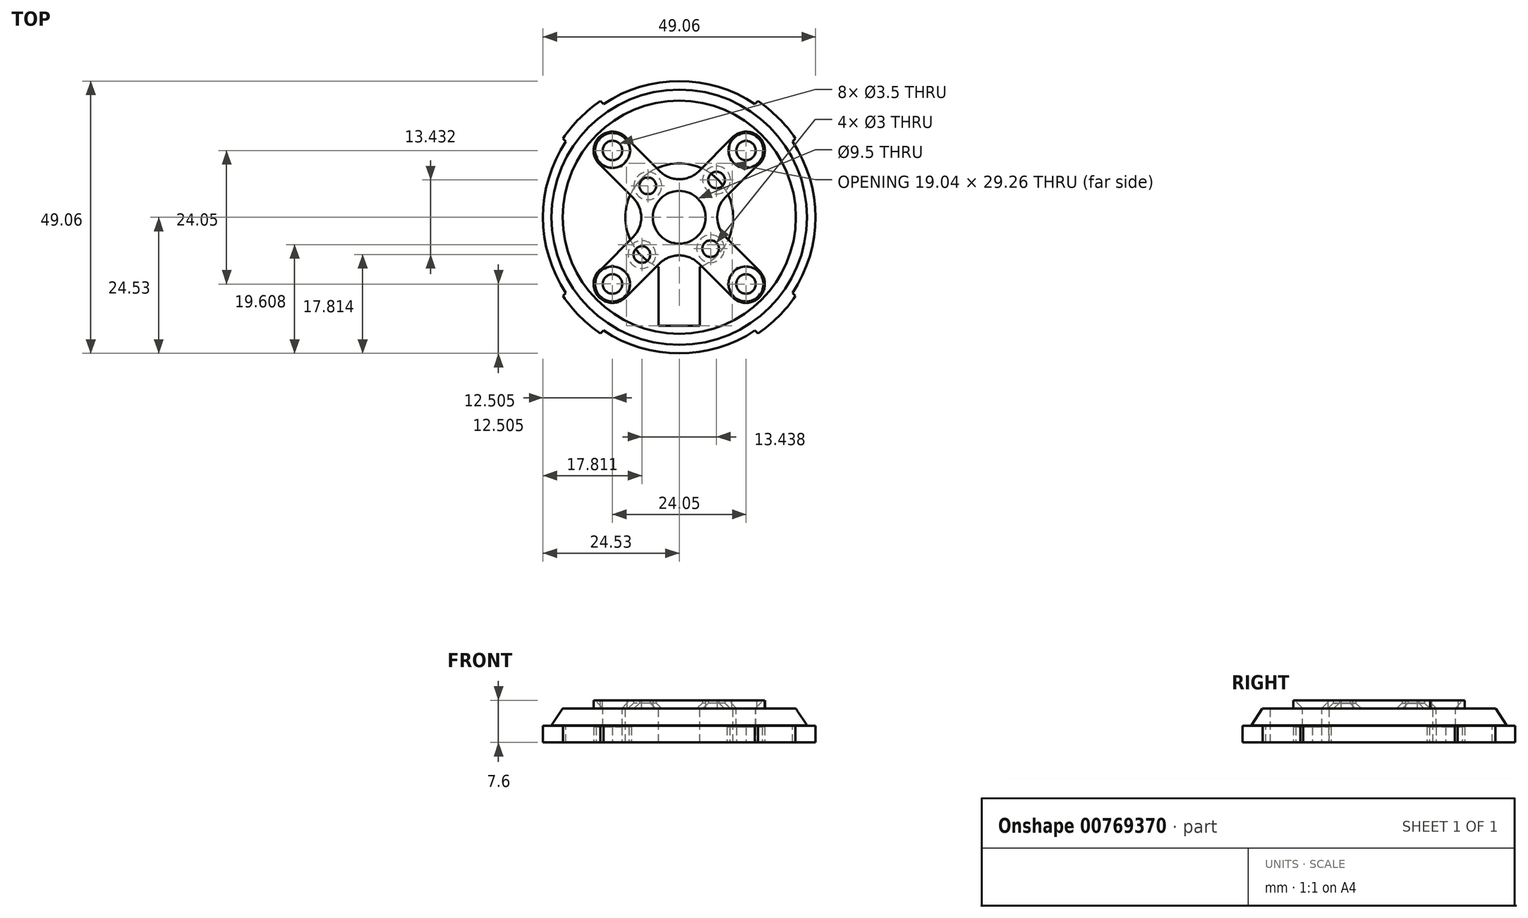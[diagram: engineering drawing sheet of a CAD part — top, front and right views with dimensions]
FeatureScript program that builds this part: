
annotation { "Feature Type Name" : "Feature", "Feature Type Description" : "" }
export const myFeature = defineFeature(function(context is Context, id is Id, definition is map)
    precondition{}
    {
        {
            var Q0;
            Q0=qCreatedBy(makeId("Top.planeOp"),FACE);
            var sketch = newSketch(context, id + "F0", { "sketchPlane" : qUnion([Q0])});
            skCircle(sketch, "E0", {"center": v(0, 0) * mm, "radius": 24.53 * mm});
            skSolve(sketch);
        }
        {
            var Q0;
            Q0=qSketchRegion(id+"F0",true);
            extrude(context, id + "F1", {"entities" : qUnion([Q0]), "oppositeDirection" : true, "depth" : 3 * mm});
        }
        {
            var Q0;
            Q0=makeQuery(id+"F1.opExtrude","CAP_FACE",FACE,{"disambiguationData":[OSD([sQuery(id+"F0.wireOp",EDGE,"E0")])],"isStart":true});
            var sketch = newSketch(context, id + "F2", { "sketchPlane" : qUnion([Q0])});
            skCircle(sketch, "E1", {"center": v(0, 0) * mm, "radius": 23 * mm});
            skSolve(sketch);
        }
        {
            var Q0;
            Q0=qSketchRegion(id+"F2",true);
            extrude(context, id + "F3", {"entities" : qUnion([Q0]), "operationType" : NewBodyOperationType.ADD, "depth" : 3.1 * mm});
        }
        {
            var Q0;
            Q0=makeQuery(id+"F3.opExtrude","CAP_EDGE",EDGE,{"disambiguationData":[OSD([sQuery(id+"F2.wireOp",EDGE,"E1")])],"isStart":false});
            chamfer(context, id + "F4", {"entities" : qUnion([Q0]), "chamferType" : ChamferType.TWO_OFFSETS, "width1" : 2 * mm, "oppositeDirection" : false, "width2" : 3 * mm, "tangentPropagation" : true});
        }
        {
            var Q0;
            Q0=makeQuery(id+"F3.opExtrude","CAP_FACE",FACE,{"disambiguationData":[OSD([sQuery(id+"F2.wireOp",EDGE,"E1")])],"isStart":false});
            var sketch = newSketch(context, id + "F5", { "sketchPlane" : qUnion([Q0])});
            skLineSegment(sketch, "E2.bottom", {"start": v(-12.02, 12.02) * mm, "end": v(12.02, 12.02) * mm, "construction": true});
            skLineSegment(sketch, "E2.top", {"start": v(-12.02, -12.02) * mm, "end": v(12.02, -12.02) * mm, "construction": true});
            skLineSegment(sketch, "E2.left", {"start": v(-12.02, 12.02) * mm, "end": v(-12.02, -12.02) * mm, "construction": true});
            skLineSegment(sketch, "E2.right", {"start": v(12.02, 12.02) * mm, "end": v(12.02, -12.02) * mm, "construction": true});
            skPoint(sketch, "E2.middle", {"position": v(0, 0) * mm});
            skCircle(sketch, "E3", {"center": v(-12.02, 12.02) * mm, "radius": 1.75 * mm});
            skCircle(sketch, "E4.1.0", {"center": v(-12.02, -12.02) * mm, "radius": 1.75 * mm});
            skCircle(sketch, "E4.2.0", {"center": v(12.02, -12.02) * mm, "radius": 1.75 * mm});
            skCircle(sketch, "E4.3.0", {"center": v(12.02, 12.02) * mm, "radius": 1.75 * mm});
            skSolve(sketch);
        }
        {
            var Q0;
            Q0=makeQuery(id+"F5.imprint","IMPRINT",FACE,{"disambiguationData":[TD([[makeQuery(id+"F5.imprint","IMPRINT",EDGE,{"derivedFrom":sQuery(id+"F5.wireOp",EDGE,"E3")}),-1.0]])]});
            var sketch = newSketch(context, id + "F6", { "sketchPlane" : qUnion([Q0])});
            skArc(sketch, "E5", {"start": v(3.71, -8.97) * mm, "mid": v(0, 9.7) * mm, "end": v(-3.71, -8.97) * mm});
            skLineSegment(sketch, "E6.top", {"start": v(-3.71, -19.55) * mm, "end": v(3.71, -19.55) * mm});
            skLineSegment(sketch, "E6.left", {"start": v(-3.71, -8.97) * mm, "end": v(-3.71, -19.55) * mm});
            skLineSegment(sketch, "E6.right", {"start": v(3.71, -8.97) * mm, "end": v(3.71, -19.55) * mm});
            skSolve(sketch);
        }
        {
            var Q0;
            Q0=qSketchRegion(id+"F6",true);
            extrude(context, id + "F7", {"entities" : qUnion([Q0]), "operationType" : NewBodyOperationType.REMOVE, "oppositeDirection" : true, "depth" : 25 * mm});
        }
        {
            var Q0;
            Q0=qSketchRegion(id+"F5",true);
            extrude(context, id + "F8", {"entities" : qUnion([Q0]), "operationType" : NewBodyOperationType.REMOVE, "oppositeDirection" : true, "depth" : 25 * mm});
        }
        {
            var Q0;
            Q0=makeQuery(id+"F3.opExtrude","CAP_FACE",FACE,{"disambiguationData":[OSD([sQuery(id+"F2.wireOp",EDGE,"E1")])],"isStart":false});
            var sketch = newSketch(context, id + "F9", { "sketchPlane" : qUnion([Q0])});
            skArc(sketch, "E7", {"start": v(-9.44, 14.24) * mm, "mid": v(-14.4, 14.46) * mm, "end": v(-14.3, 9.5) * mm});
            skArc(sketch, "E8.1.0", {"start": v(-13.89, -9.17) * mm, "mid": v(-14.66, -14.17) * mm, "end": v(-9.62, -14.42) * mm});
            skArc(sketch, "E8.2.0", {"start": v(9.61, -14.43) * mm, "mid": v(14.42, -14.43) * mm, "end": v(14.42, -9.62) * mm});
            skArc(sketch, "E8.3.0", {"start": v(13.94, 9.2) * mm, "mid": v(14.56, 14.28) * mm, "end": v(9.45, 14.24) * mm});
            skPoint(sketch, "E8.center", {"position": v(0, 0) * mm});
            skLineSegment(sketch, "E9", {"start": v(-14.3, 9.5) * mm, "end": v(-8.3, 3.5) * mm});
            skLineSegment(sketch, "E10", {"start": v(-9.8, 14.6) * mm, "end": v(-3.52, 8.32) * mm});
            skLineSegment(sketch, "E11", {"start": v(13.94, 9.2) * mm, "end": v(8.3, 3.56) * mm});
            skLineSegment(sketch, "E12", {"start": v(9.8, 14.59) * mm, "end": v(3.56, 8.33) * mm});
            skLineSegment(sketch, "E13.trimOffspring", {"start": v(-8.3, -3.56) * mm, "end": v(-13.89, -9.17) * mm});
            skLineSegment(sketch, "E14.trimOffspring", {"start": v(3.52, -8.33) * mm, "end": v(9.61, -14.43) * mm});
            skLineSegment(sketch, "E15.trimOffspring", {"start": v(-3.55, -8.34) * mm, "end": v(-9.62, -14.42) * mm});
            skLineSegment(sketch, "E16.trimOffspring", {"start": v(8.31, -3.5) * mm, "end": v(14.42, -9.62) * mm});
            skCircle(sketch, "E17", {"center": v(-12.02, 12.02) * mm, "radius": 1.75 * mm});
            skCircle(sketch, "E18.1.0", {"center": v(-12.02, -12.02) * mm, "radius": 1.75 * mm});
            skCircle(sketch, "E18.2.0", {"center": v(12.02, -12.02) * mm, "radius": 1.75 * mm});
            skCircle(sketch, "E18.3.0", {"center": v(12.02, 12.02) * mm, "radius": 1.75 * mm});
            skCircle(sketch, "E19", {"center": v(0, 0) * mm, "radius": 4.75 * mm});
            skPoint(sketch, "E20.visualSharp", {"position": v(-4.77, -0.03) * mm});
            skArc(sketch, "E20.filletArc", {"start": v(-8.3, -3.56) * mm, "mid": v(-6.84, -0.03) * mm, "end": v(-8.3, 3.5) * mm});
            skPoint(sketch, "E21.visualSharp", {"position": v(4.78, 0.02) * mm});
            skArc(sketch, "E21.filletArc", {"start": v(8.3, 3.56) * mm, "mid": v(6.85, 0.02) * mm, "end": v(8.31, -3.5) * mm});
            skPoint(sketch, "E22.visualSharp", {"position": v(0.02, 4.78) * mm});
            skArc(sketch, "E22.filletArc", {"start": v(-3.52, 8.32) * mm, "mid": v(0.02, 6.86) * mm, "end": v(3.56, 8.33) * mm});
            skPoint(sketch, "E23.visualSharp", {"position": v(-0.02, -4.79) * mm});
            skArc(sketch, "E23.filletArc", {"start": v(3.52, -8.33) * mm, "mid": v(-0.02, -6.87) * mm, "end": v(-3.55, -8.34) * mm});
            skLineSegment(sketch, "E24", {"start": v(0, 0) * mm, "end": v(-12.02, 12.02) * mm, "construction": true});
            skCircle(sketch, "E25", {"center": v(-5.66, 5.66) * mm, "radius": 1.5 * mm});
            skLineSegment(sketch, "E26", {"start": v(0, 0) * mm, "end": v(12.02, -12.02) * mm, "construction": true});
            skLineSegment(sketch, "E27", {"start": v(0, 0) * mm, "end": v(-12.02, -12.02) * mm, "construction": true});
            skLineSegment(sketch, "E28", {"start": v(0, 0) * mm, "end": v(12.02, 12.02) * mm, "construction": true});
            skCircle(sketch, "E29", {"center": v(5.66, -5.66) * mm, "radius": 1.5 * mm});
            skCircle(sketch, "E30", {"center": v(-6.72, -6.72) * mm, "radius": 1.5 * mm});
            skCircle(sketch, "E31", {"center": v(6.72, 6.72) * mm, "radius": 1.5 * mm});
            skSolve(sketch);
        }
        {
            var Q0;
            Q0=qSketchRegion(id+"F9",true);
            extrude(context, id + "F10", {"entities" : qUnion([Q0]), "depth" : 1.5 * mm});
        }
        {
            var Q0;
            Q0=makeQuery(id+"F10.opExtrude","CAP_EDGE",EDGE,{"disambiguationData":[OSD([sQuery(id+"F9.wireOp",EDGE,"E17")])],"isStart":false});
            var Q1;
            Q1=makeQuery(id+"F10.opExtrude","CAP_EDGE",EDGE,{"disambiguationData":[OSD([sQuery(id+"F9.wireOp",EDGE,"E18.3.0")])],"isStart":false});
            var Q2;
            Q2=makeQuery(id+"F10.opExtrude","CAP_EDGE",EDGE,{"disambiguationData":[OSD([sQuery(id+"F9.wireOp",EDGE,"E18.1.0")])],"isStart":false});
            var Q3;
            Q3=makeQuery(id+"F10.opExtrude","CAP_EDGE",EDGE,{"disambiguationData":[OSD([sQuery(id+"F9.wireOp",EDGE,"E18.2.0")])],"isStart":false});
            chamfer(context, id + "F11", {"entities" : qUnion([Q0, Q1, Q2, Q3]), "width" : 1.4 * mm, "tangentPropagation" : true});
        }
        {
            var Q0;
            Q0=makeQuery(id+"F1.opExtrude","CAP_FACE",FACE,{"disambiguationData":[OSD([sQuery(id+"F0.wireOp",EDGE,"E0")])],"isStart":false});
            var sketch = newSketch(context, id + "F12", { "sketchPlane" : qUnion([Q0])});
            skCircle(sketch, "E32.cCircle", {"center": v(12.02, 12.02) * mm, "radius": 2.94 * mm, "construction": true});
            skLineSegment(sketch, "E32.0", {"start": v(13.72, 9.08) * mm, "end": v(10.32, 9.08) * mm});
            skLineSegment(sketch, "E32.1", {"start": v(10.32, 9.08) * mm, "end": v(8.62, 12.02) * mm});
            skLineSegment(sketch, "E32.2", {"start": v(8.62, 12.02) * mm, "end": v(10.32, 14.97) * mm});
            skLineSegment(sketch, "E32.3", {"start": v(10.32, 14.97) * mm, "end": v(13.72, 14.97) * mm});
            skLineSegment(sketch, "E32.4", {"start": v(13.72, 14.97) * mm, "end": v(15.42, 12.02) * mm});
            skLineSegment(sketch, "E32.5", {"start": v(15.42, 12.02) * mm, "end": v(13.72, 9.08) * mm});
            skPoint(sketch, "E32.0.midPoint", {"position": v(12.02, 9.08) * mm});
            skLineSegment(sketch, "E33.1.0", {"start": v(-12.02, 8.62) * mm, "end": v(-14.97, 10.32) * mm});
            skLineSegment(sketch, "E33.1.1", {"start": v(-14.97, 10.32) * mm, "end": v(-14.97, 13.72) * mm});
            skLineSegment(sketch, "E33.1.2", {"start": v(-14.97, 13.72) * mm, "end": v(-12.02, 15.42) * mm});
            skLineSegment(sketch, "E33.1.3", {"start": v(-12.02, 15.42) * mm, "end": v(-9.08, 13.72) * mm});
            skLineSegment(sketch, "E33.1.4", {"start": v(-9.08, 13.72) * mm, "end": v(-9.08, 10.32) * mm});
            skLineSegment(sketch, "E33.1.5", {"start": v(-9.08, 10.32) * mm, "end": v(-12.02, 8.62) * mm});
            skLineSegment(sketch, "E33.2.0", {"start": v(-8.62, -12.02) * mm, "end": v(-10.32, -14.97) * mm});
            skLineSegment(sketch, "E33.2.1", {"start": v(-10.32, -14.97) * mm, "end": v(-13.72, -14.97) * mm});
            skLineSegment(sketch, "E33.2.2", {"start": v(-13.72, -14.97) * mm, "end": v(-15.42, -12.02) * mm});
            skLineSegment(sketch, "E33.2.3", {"start": v(-15.42, -12.02) * mm, "end": v(-13.72, -9.08) * mm});
            skLineSegment(sketch, "E33.2.4", {"start": v(-13.72, -9.08) * mm, "end": v(-10.32, -9.08) * mm});
            skLineSegment(sketch, "E33.2.5", {"start": v(-10.32, -9.08) * mm, "end": v(-8.62, -12.02) * mm});
            skLineSegment(sketch, "E33.3.0", {"start": v(12.02, -8.62) * mm, "end": v(14.97, -10.32) * mm});
            skLineSegment(sketch, "E33.3.1", {"start": v(14.97, -10.32) * mm, "end": v(14.97, -13.72) * mm});
            skLineSegment(sketch, "E33.3.2", {"start": v(14.97, -13.72) * mm, "end": v(12.02, -15.42) * mm});
            skLineSegment(sketch, "E33.3.3", {"start": v(12.02, -15.42) * mm, "end": v(9.08, -13.72) * mm});
            skLineSegment(sketch, "E33.3.4", {"start": v(9.08, -13.72) * mm, "end": v(9.08, -10.32) * mm});
            skLineSegment(sketch, "E33.3.5", {"start": v(9.08, -10.32) * mm, "end": v(12.02, -8.62) * mm});
            skPoint(sketch, "E33.center", {"position": v(0, 0) * mm});
            skSolve(sketch);
        }
        {
            var Q0;
            Q0=qSketchRegion(id+"F12",true);
            extrude(context, id + "F13", {"entities" : qUnion([Q0]), "operationType" : NewBodyOperationType.REMOVE, "oppositeDirection" : true, "depth" : 2.8 * mm});
        }
        {
            var Q0;
            Q0=makeQuery(id+"F1.opExtrude","CAP_FACE",FACE,{"disambiguationData":[OSD([sQuery(id+"F0.wireOp",EDGE,"E0")])],"isStart":true});
            var sketch = newSketch(context, id + "F14", { "sketchPlane" : qUnion([Q0])});
            skArc(sketch, "E34.0", {"start": v(-20.93, -14.18) * mm, "mid": v(-17.88, -17.88) * mm, "end": v(-14.18, -20.93) * mm});
            skLineSegment(sketch, "E35.left", {"start": v(-14.18, 20.93) * mm, "end": v(0, 6.75) * mm});
            skLineSegment(sketch, "E35.right", {"start": v(-20.93, 14.18) * mm, "end": v(-6.75, 0) * mm});
            skLineSegment(sketch, "E36.MirrorCS", {"start": v(14.18, 20.93) * mm, "end": v(0, 6.75) * mm});
            skLineSegment(sketch, "E37.MirrorCS", {"start": v(20.93, 14.18) * mm, "end": v(6.75, 0) * mm});
            skLineSegment(sketch, "E38.trimOffspring", {"start": v(-6.75, 0) * mm, "end": v(-20.93, -14.18) * mm});
            skLineSegment(sketch, "E39.trimOffspring", {"start": v(0, -6.75) * mm, "end": v(14.18, -20.93) * mm});
            skLineSegment(sketch, "E40.trimOffspring", {"start": v(0, -6.75) * mm, "end": v(-14.18, -20.93) * mm});
            skLineSegment(sketch, "E41.trimOffspring", {"start": v(6.75, 0) * mm, "end": v(20.93, -14.18) * mm});
            skPoint(sketch, "E35.bottom.end.orphan", {"position": v(-22.7, 15.96) * mm});
            skArc(sketch, "E42.trimOffspring", {"start": v(14.18, -20.93) * mm, "mid": v(17.88, -17.88) * mm, "end": v(20.93, -14.18) * mm});
            skPoint(sketch, "E35.top.end.orphan", {"position": v(15.96, -22.7) * mm});
            skPoint(sketch, "E43.orphan", {"position": v(22.7, -15.96) * mm});
            skPoint(sketch, "E44.orphan", {"position": v(-15.96, 22.7) * mm});
            skArc(sketch, "E45.trimOffspring", {"start": v(-14.18, 20.93) * mm, "mid": v(-17.88, 17.88) * mm, "end": v(-20.93, 14.18) * mm});
            skArc(sketch, "E46.trimOffspring", {"start": v(20.93, 14.18) * mm, "mid": v(17.88, 17.88) * mm, "end": v(14.18, 20.93) * mm});
            skSolve(sketch);
        }
        {
            var Q0;
            {var subQ0=sQuery(id+"F14.wireOp",EDGE,"E45.trimOffspring");Q0=makeQuery(id+"F14.imprint","IMPRINT",FACE,{"disambiguationData":[TD([[makeQuery(id+"F14.imprint","IMPRINT",EDGE,{"derivedFrom":subQ0}),1.0]])]});}
            var Q1;
            {var subQ0=sQuery(id+"F14.wireOp",EDGE,"E46.trimOffspring");Q1=makeQuery(id+"F14.imprint","IMPRINT",FACE,{"disambiguationData":[TD([[makeQuery(id+"F14.imprint","IMPRINT",EDGE,{"derivedFrom":subQ0}),1.0]])]});}
            var Q2;
            {var subQ0=sQuery(id+"F14.wireOp",EDGE,"E34.0");Q2=makeQuery(id+"F14.imprint","IMPRINT",FACE,{"disambiguationData":[TD([[makeQuery(id+"F14.imprint","IMPRINT",EDGE,{"derivedFrom":subQ0}),1.0]])]});}
            var Q3;
            {var subQ0=sQuery(id+"F14.wireOp",EDGE,"E42.trimOffspring");Q3=makeQuery(id+"F14.imprint","IMPRINT",FACE,{"disambiguationData":[TD([[makeQuery(id+"F14.imprint","IMPRINT",EDGE,{"derivedFrom":subQ0}),1.0]])]});}
            var Q4;
            Q4=makeQuery(id+"F1.opExtrude","CAP_FACE",FACE,{"disambiguationData":[OSD([sQuery(id+"F0.wireOp",EDGE,"E0")])],"isStart":false});
            extrude(context, id + "F15", {"entities" : qUnion([Q0, Q1, Q2, Q3]), "operationType" : NewBodyOperationType.ADD, "endBound" : BoundingType.UP_TO_SURFACE, "oppositeDirection" : true, "endBoundEntityFace" : qUnion([Q4]), "depth" : 25 * mm});
        }
        {
            var Q0;
            Q0=makeQuery(id+"F10.opExtrude","CAP_EDGE",EDGE,{"disambiguationData":[OSD([sQuery(id+"F9.wireOp",EDGE,"E30")])],"isStart":true});
            var Q1;
            Q1=makeQuery(id+"F10.opExtrude","CAP_EDGE",EDGE,{"disambiguationData":[OSD([sQuery(id+"F9.wireOp",EDGE,"E25")])],"isStart":true});
            var Q2;
            Q2=makeQuery(id+"F10.opExtrude","CAP_EDGE",EDGE,{"disambiguationData":[OSD([sQuery(id+"F9.wireOp",EDGE,"E29")])],"isStart":true});
            var Q3;
            Q3=makeQuery(id+"F10.opExtrude","CAP_EDGE",EDGE,{"disambiguationData":[OSD([sQuery(id+"F9.wireOp",EDGE,"E31")])],"isStart":true});
            chamfer(context, id + "F16", {"entities" : qUnion([Q0, Q1, Q2, Q3]), "width" : 1 * mm, "tangentPropagation" : true});
        }
    });
